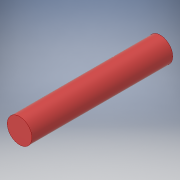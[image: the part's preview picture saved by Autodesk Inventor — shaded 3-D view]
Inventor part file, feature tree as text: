
AUTODESK INVENTOR PART (.ipt)
format: ipt  version: 2019 (Build 230136000, 136)  size: 94,208 bytes
history: native  units: mm
features: extrude x1, sketch x1
ambient origin geometry x8: Origin, YZ Plane, XZ Plane, XY Plane, X Axis, Y Axis, Z Axis, Center Point
bodies: Solid1 (feature_tree)
feature tree (2):
  extrude  "Extrusion1"  Depth=20.0mm TaperAngle=0.0deg
  sketch  "Sketch1"  dims[d0=3.5mm d1=20.0mm d2=0.0mm]
